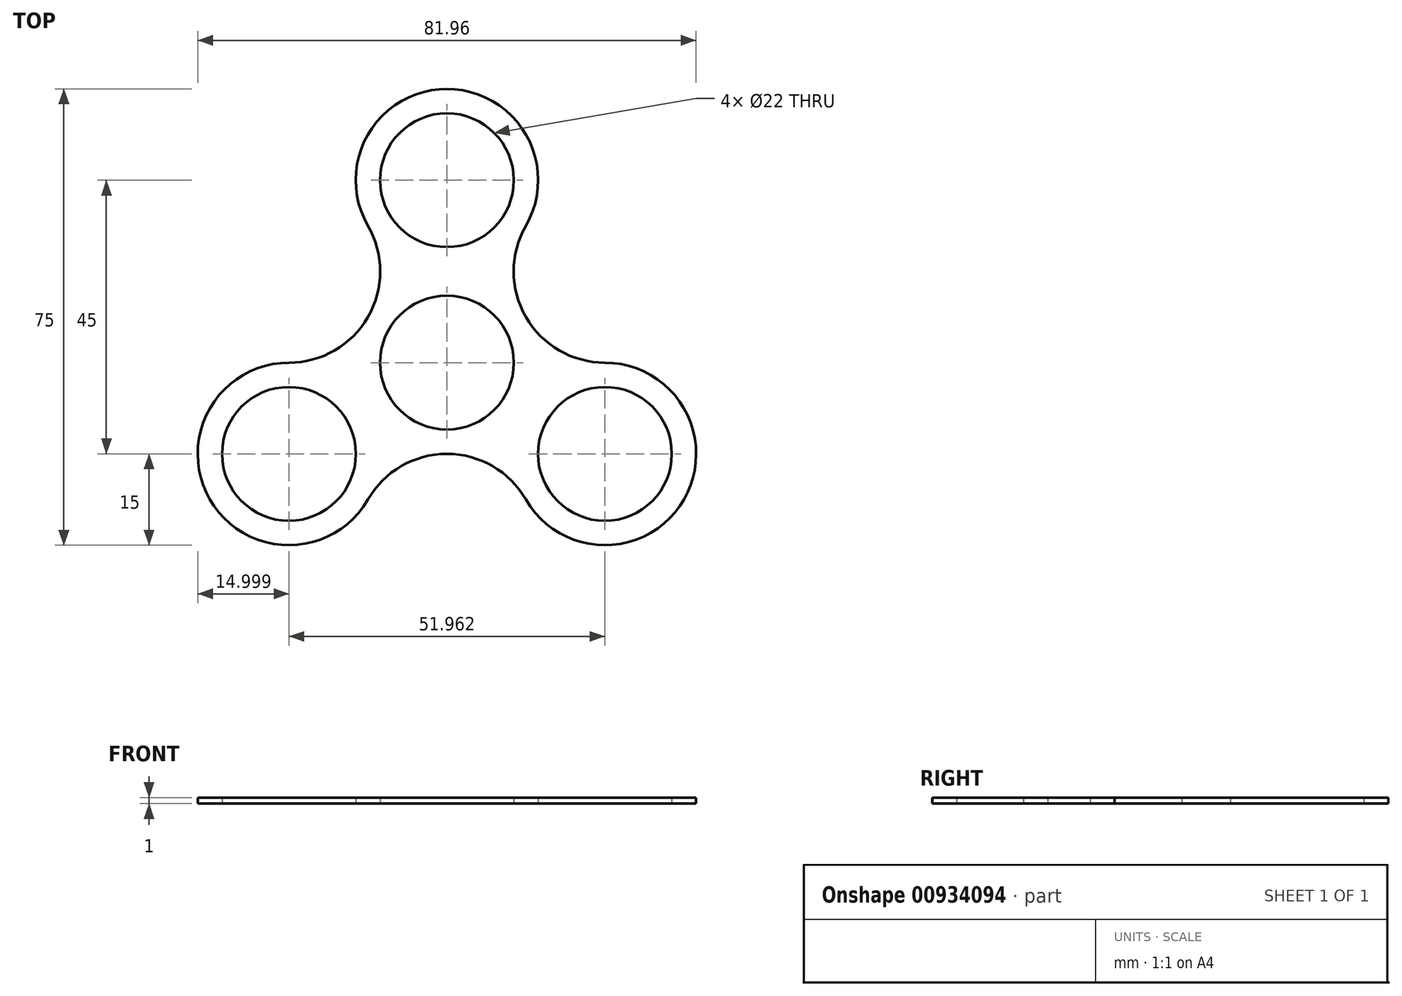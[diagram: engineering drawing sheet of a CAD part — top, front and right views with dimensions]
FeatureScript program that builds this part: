
annotation { "Feature Type Name" : "Feature", "Feature Type Description" : "" }
export const myFeature = defineFeature(function(context is Context, id is Id, definition is map)
    precondition{}
    {
        {
            var Q0;
            Q0=qCreatedBy(makeId("Top.planeOp"),FACE);
            var sketch = newSketch(context, id + "F0", { "sketchPlane" : qUnion([Q0])});
            skLineSegment(sketch, "E0.0", {"start": v(0, 30) * mm, "end": v(25.98, -15) * mm, "construction": true});
            skLineSegment(sketch, "E0.1", {"start": v(25.98, -15) * mm, "end": v(-25.98, -15) * mm, "construction": true});
            skLineSegment(sketch, "E0.2", {"start": v(-25.98, -15) * mm, "end": v(0, 30) * mm, "construction": true});
            skCircle(sketch, "E1", {"center": v(0, 30) * mm, "radius": 11 * mm});
            skCircle(sketch, "E2", {"center": v(25.98, -15) * mm, "radius": 11 * mm});
            skCircle(sketch, "E3", {"center": v(-25.98, -15) * mm, "radius": 11 * mm});
            skLineSegment(sketch, "E4", {"start": v(-25.98, -15) * mm, "end": v(0, 0) * mm, "construction": true});
            skLineSegment(sketch, "E5", {"start": v(0, 0) * mm, "end": v(25.98, -15) * mm, "construction": true});
            skLineSegment(sketch, "E6", {"start": v(0, 0) * mm, "end": v(0, 30) * mm, "construction": true});
            skCircle(sketch, "E7", {"center": v(0, 0) * mm, "radius": 11 * mm});
            skCircle(sketch, "E8", {"center": v(0, 30) * mm, "radius": 15 * mm});
            skCircle(sketch, "E9", {"center": v(25.98, -15) * mm, "radius": 15 * mm});
            skCircle(sketch, "E10", {"center": v(-25.98, -15) * mm, "radius": 15 * mm});
            skLineSegment(sketch, "E11", {"start": v(0, 0) * mm, "end": v(-13, 7.5) * mm, "construction": true});
            skLineSegment(sketch, "E12", {"start": v(0, 0) * mm, "end": v(13, 7.5) * mm, "construction": true});
            skLineSegment(sketch, "E13", {"start": v(0, 0) * mm, "end": v(0, -15) * mm, "construction": true});
            skArc(sketch, "E14", {"start": v(-25.98, 0) * mm, "mid": v(-13, 7.5) * mm, "end": v(-13, 22.5) * mm});
            skPoint(sketch, "E14.second.point", {"position": v(-13, 22.5) * mm});
            skPoint(sketch, "E14.third.point", {"position": v(-25.98, 0) * mm});
            skArc(sketch, "E15", {"start": v(13, 22.5) * mm, "mid": v(13, 7.5) * mm, "end": v(25.98, 0) * mm});
            skPoint(sketch, "E15.second.point", {"position": v(13, 22.5) * mm});
            skPoint(sketch, "E15.third.point", {"position": v(25.98, 0) * mm});
            skArc(sketch, "E16", {"start": v(13, -22.5) * mm, "mid": v(0, -15) * mm, "end": v(-13, -22.5) * mm});
            skPoint(sketch, "E16.second.point", {"position": v(-13, -22.5) * mm});
            skPoint(sketch, "E16.third.point", {"position": v(13, -22.5) * mm});
            skSolve(sketch);
        }
        {
            var Q0;
            Q0=makeQuery(id+"F0.imprint","IMPRINT",FACE,{"disambiguationData":[TD([[makeQuery(id+"F0.imprint","IMPRINT",EDGE,{"derivedFrom":sQuery(id+"F0.wireOp",EDGE,"E3")}),-1.0]])]});
            var Q1;
            Q1=makeQuery(id+"F0.imprint","IMPRINT",FACE,{"disambiguationData":[TD([[makeQuery(id+"F0.imprint","IMPRINT",EDGE,{"derivedFrom":sQuery(id+"F0.wireOp",EDGE,"E7")}),-1.0]])]});
            var Q2;
            Q2=makeQuery(id+"F0.imprint","IMPRINT",FACE,{"disambiguationData":[TD([[makeQuery(id+"F0.imprint","IMPRINT",EDGE,{"derivedFrom":sQuery(id+"F0.wireOp",EDGE,"E2")}),-1.0]])]});
            var Q3;
            Q3=makeQuery(id+"F0.imprint","IMPRINT",FACE,{"disambiguationData":[TD([[makeQuery(id+"F0.imprint","IMPRINT",EDGE,{"derivedFrom":sQuery(id+"F0.wireOp",EDGE,"E1")}),-1.0]])]});
            extrude(context, id + "F1", {"entities" : qUnion([Q0, Q1, Q2, Q3]), "depth" : 1 * mm, "offsetDistance" : 25 * mm});
        }
    });
